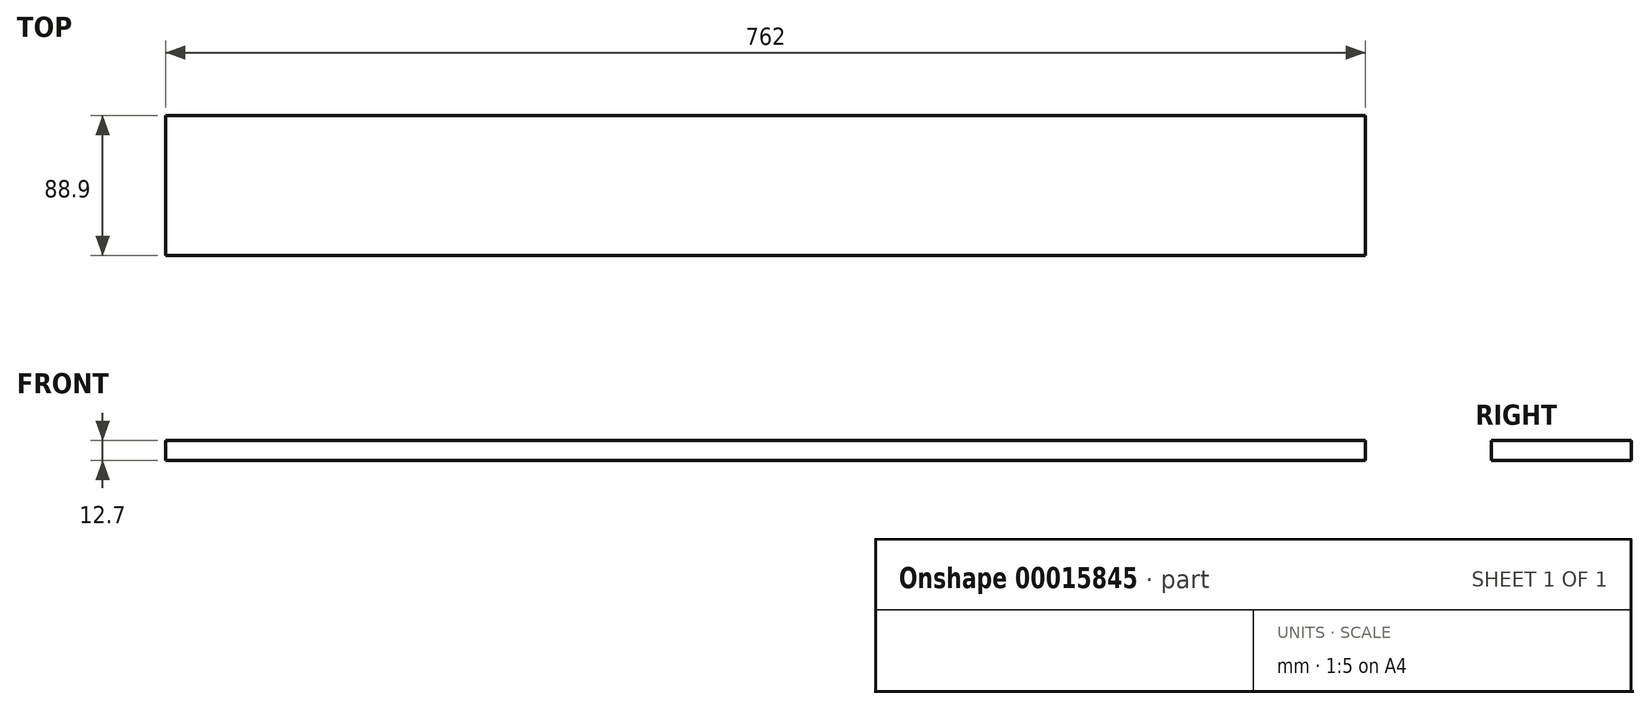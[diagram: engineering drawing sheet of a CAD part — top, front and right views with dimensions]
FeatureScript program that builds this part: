
annotation { "Feature Type Name" : "Feature", "Feature Type Description" : "" }
export const myFeature = defineFeature(function(context is Context, id is Id, definition is map)
    precondition{}
    {
        {
            var Q0;
            Q0=qCreatedBy(makeId("Top.planeOp"),FACE);
            var sketch = newSketch(context, id + "F0", { "sketchPlane" : qUnion([Q0])});
            skLineSegment(sketch, "E0.bottom", {"start": v(0, 0) * mm, "end": v(762, 0) * mm});
            skLineSegment(sketch, "E0.top", {"start": v(0, -88.9) * mm, "end": v(762, -88.9) * mm});
            skLineSegment(sketch, "E0.left", {"start": v(0, 0) * mm, "end": v(0, -88.9) * mm});
            skLineSegment(sketch, "E0.right", {"start": v(762, 0) * mm, "end": v(762, -88.9) * mm});
            skSolve(sketch);
        }
        {
            var Q0;
            Q0 = qSketchRegion(id + "F0", true);
            extrude(context, id + "F1", {"entities" : qUnion([Q0]), "depth" : 12.7 * mm});
        }
    });
